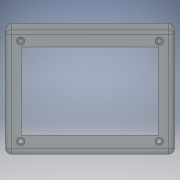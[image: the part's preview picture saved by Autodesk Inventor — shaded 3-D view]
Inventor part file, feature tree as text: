
AUTODESK INVENTOR PART (.ipt)
format: ipt  version: 2019 (Build 230136000, 136)  size: 262,144 bytes
history: native  units: mm
features: extrude x10, sketch x10, projected_geometry x3, other x1, fillet x1, imported_body x1
ambient origin geometry x8: Origin, YZ Plane, XZ Plane, XY Plane, X Axis, Y Axis, Z Axis, Center Point
bodies: Body1 (feature_tree)
feature tree (26):
  other  "實體1"
  extrude  "擠出1"  TaperAngle=0.0deg  [1 undecoded]
  extrude  "擠出2"  Depth=4.5mm TaperAngle=0.0deg
  extrude  "擠出3"  Depth=1.5mm TaperAngle=0.0deg
  extrude  "擠出4"  Depth=1.5mm TaperAngle=0.0deg
  extrude  "擠出5"  TaperAngle=0.0deg  [1 undecoded]
  fillet  "圓角1"  [1 undecoded]
  extrude  "擠出7"  Depth=14.0mm
  extrude  "擠出8"  Depth=20.0mm
  extrude  "擠出9"  Depth=3.0mm TaperAngle=0.0deg
  extrude  "擠出10"  Depth=1.0mm
  extrude  "擠出11"  Depth=2.5mm TaperAngle=0.0deg
  sketch  "草圖2"
  sketch  "草圖3"
  projected_geometry  "投影迴路1"
  sketch  "草圖4"
  sketch  "草圖5"
  projected_geometry  "投影迴路2"
  sketch  "草圖7"
  sketch  "草圖10"
  sketch  "草圖11"
  sketch  "草圖12"
  sketch  "草圖13"
  sketch  "草圖14"
  projected_geometry  "投影迴路4"
  imported_body  "Base1"
note: 3 required parameter values undecoded (feature->parameter linkage not recoverable at this tier; creation-order binding heuristic only, values carry confidence <= 0.55)
